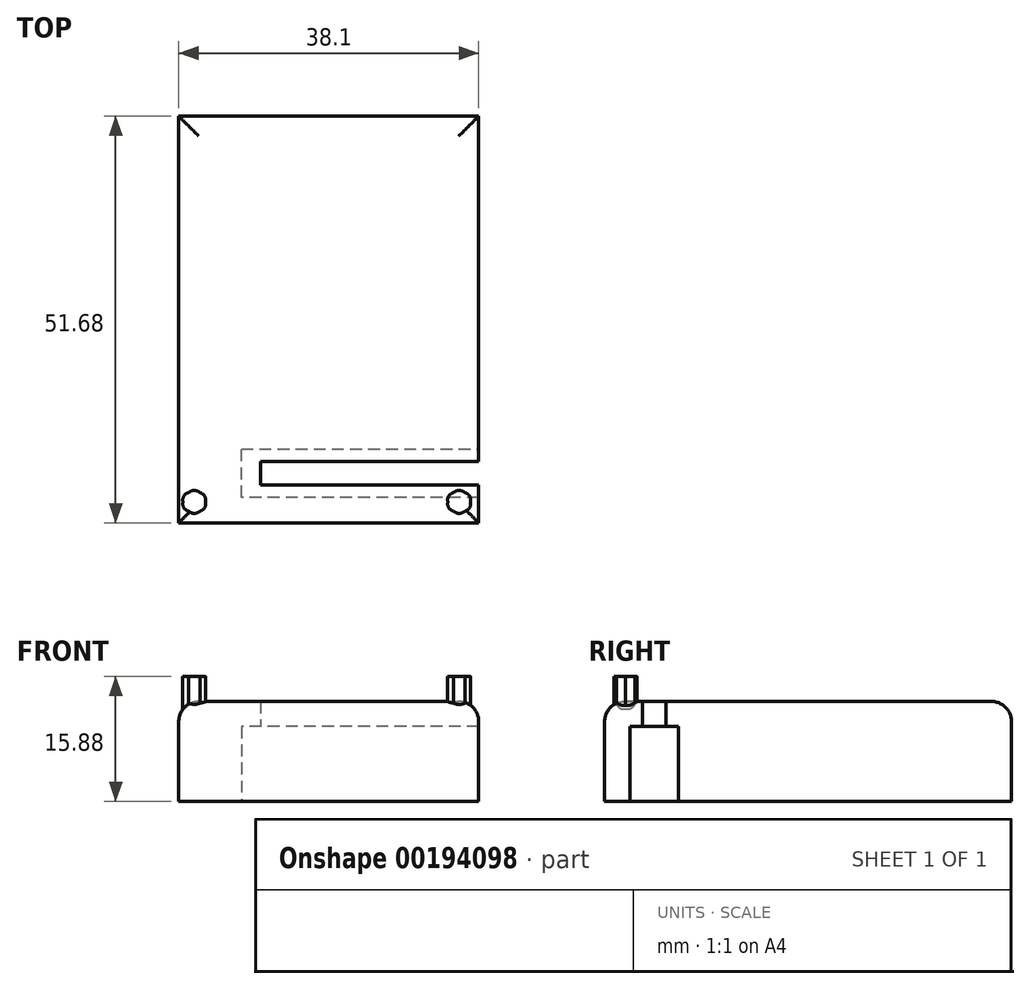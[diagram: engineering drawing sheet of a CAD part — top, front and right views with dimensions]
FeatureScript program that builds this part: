
annotation { "Feature Type Name" : "Feature", "Feature Type Description" : "" }
export const myFeature = defineFeature(function(context is Context, id is Id, definition is map)
    precondition{}
    {
        {
            var Q0;
            Q0=qCreatedBy(makeId("Top.planeOp"),FACE);
            var sketch = newSketch(context, id + "F0", { "sketchPlane" : qUnion([Q0])});
            skFitSpline(sketch, "E0", {"points": [v(-17.28, -23.17) * mm, v(-17.28, -23.66) * mm, v(-17.56, -24.1) * mm, v(-18, -24.35) * mm]});
            skFitSpline(sketch, "E1", {"points": [v(-18, -24.35) * mm, v(-18.45, -24.6) * mm, v(-19, -24.6) * mm, v(-19.44, -24.35) * mm]});
            skFitSpline(sketch, "E2", {"points": [v(-19.44, -24.35) * mm, v(-19.88, -24.1) * mm, v(-20.16, -23.66) * mm, v(-20.16, -23.17) * mm]});
            skFitSpline(sketch, "E3", {"points": [v(-20.16, -23.17) * mm, v(-20.16, -22.68) * mm, v(-19.88, -22.23) * mm, v(-19.44, -21.98) * mm]});
            skFitSpline(sketch, "E4", {"points": [v(-19.44, -21.98) * mm, v(-19, -21.74) * mm, v(-18.45, -21.74) * mm, v(-18, -21.98) * mm]});
            skFitSpline(sketch, "E5", {"points": [v(-18, -21.98) * mm, v(-17.56, -22.23) * mm, v(-17.28, -22.68) * mm, v(-17.28, -23.17) * mm]});
            skFitSpline(sketch, "E6", {"points": [v(16.37, -23.17) * mm, v(16.37, -23.66) * mm, v(16.1, -24.1) * mm, v(15.65, -24.35) * mm]});
            skFitSpline(sketch, "E7", {"points": [v(15.65, -24.35) * mm, v(15.2, -24.6) * mm, v(14.66, -24.6) * mm, v(14.21, -24.35) * mm]});
            skFitSpline(sketch, "E8", {"points": [v(14.21, -24.35) * mm, v(13.77, -24.1) * mm, v(13.5, -23.66) * mm, v(13.5, -23.17) * mm]});
            skFitSpline(sketch, "E9", {"points": [v(13.5, -23.17) * mm, v(13.5, -22.68) * mm, v(13.77, -22.23) * mm, v(14.21, -21.98) * mm]});
            skFitSpline(sketch, "E10", {"points": [v(14.21, -21.98) * mm, v(14.66, -21.74) * mm, v(15.2, -21.74) * mm, v(15.65, -21.98) * mm]});
            skFitSpline(sketch, "E11", {"points": [v(15.65, -21.98) * mm, v(16.1, -22.23) * mm, v(16.37, -22.68) * mm, v(16.37, -23.17) * mm]});
            skLineSegment(sketch, "E12", {"start": v(-10.31, -18.02) * mm, "end": v(17.41, -18.02) * mm});
            skLineSegment(sketch, "E13", {"start": v(-10.31, -21.04) * mm, "end": v(-10.31, -18.02) * mm});
            skLineSegment(sketch, "E14", {"start": v(-12.73, -16.46) * mm, "end": v(17.41, -16.46) * mm});
            skLineSegment(sketch, "E15", {"start": v(17.41, -22.6) * mm, "end": v(-12.73, -22.6) * mm});
            skLineSegment(sketch, "E16", {"start": v(-12.73, -22.6) * mm, "end": v(-12.73, -16.46) * mm});
            skLineSegment(sketch, "E17", {"start": v(-20.69, 25.84) * mm, "end": v(17.41, 25.84) * mm});
            skLineSegment(sketch, "E18", {"start": v(17.41, 24.96) * mm, "end": v(17.41, -25.84) * mm});
            skLineSegment(sketch, "E19", {"start": v(17.41, -25.84) * mm, "end": v(-20.69, -25.84) * mm});
            skLineSegment(sketch, "E20", {"start": v(-20.69, -25.84) * mm, "end": v(-20.69, 24.96) * mm});
            skLineSegment(sketch, "E21.trimOffspring", {"start": v(17.41, -21.04) * mm, "end": v(-10.31, -21.04) * mm});
            skLineSegment(sketch, "E22", {"start": v(17.41, 24.96) * mm, "end": v(17.41, 25.84) * mm});
            skLineSegment(sketch, "E23", {"start": v(-20.69, 24.96) * mm, "end": v(-20.69, 25.84) * mm});
            skSolve(sketch);
        }
        {
            var Q0;
            Q0=makeQuery(id+"F0.imprint","IMPRINT",FACE,{"disambiguationData":[TD([[makeQuery(id+"F0.imprint","IMPRINT",EDGE,{"derivedFrom":sQuery(id+"F0.wireOp",EDGE,"E0")}),1.0]])]});
            var Q1;
            {var subQ10=sQuery(id+"F0.wireOp",EDGE,"E10");Q1=makeQuery(id+"F0.imprint","IMPRINT",FACE,{"disambiguationData":[TD([[makeQuery(id+"F0.imprint","IMPRINT",EDGE,{"derivedFrom":subQ10}),1.0]])]});}
            var Q2;
            {var subQ0=sQuery(id+"F0.wireOp",EDGE,"E12");Q2=makeQuery(id+"F0.imprint","IMPRINT",FACE,{"disambiguationData":[TD([[makeQuery(id+"F0.imprint","IMPRINT",EDGE,{"derivedFrom":subQ0}),-1.0]])]});}
            var Q3;
            {var subQ6=sQuery(id+"F0.wireOp",EDGE,"E6");Q3=makeQuery(id+"F0.imprint","IMPRINT",FACE,{"disambiguationData":[TD([[makeQuery(id+"F0.imprint","IMPRINT",EDGE,{"derivedFrom":subQ6}),-1.0]])]});}
            var Q4;
            {var subQ0=sQuery(id+"F0.wireOp",EDGE,"E10");Q4=makeQuery(id+"F0.imprint","IMPRINT",FACE,{"disambiguationData":[TD([[makeQuery(id+"F0.imprint","IMPRINT",EDGE,{"derivedFrom":subQ0}),-1.0]])]});}
            var Q5;
            Q5=makeQuery(id+"F0.imprint","IMPRINT",FACE,{"disambiguationData":[TD([[makeQuery(id+"F0.imprint","IMPRINT",EDGE,{"derivedFrom":sQuery(id+"F0.wireOp",EDGE,"E0")}),-1.0]])]});
            extrude(context, id + "F1", {"entities" : qUnion([Q0, Q1, Q2, Q3, Q4, Q5]), "depth" : 12.7 * mm});
        }
        {
            var Q0;
            {var subQ10=sQuery(id+"F0.wireOp",EDGE,"E10");Q0=makeQuery(id+"F0.imprint","IMPRINT",FACE,{"disambiguationData":[TD([[makeQuery(id+"F0.imprint","IMPRINT",EDGE,{"derivedFrom":subQ10}),1.0]])]});}
            var Q1;
            {var subQ0=sQuery(id+"F0.wireOp",EDGE,"E10");Q1=makeQuery(id+"F0.imprint","IMPRINT",FACE,{"disambiguationData":[TD([[makeQuery(id+"F0.imprint","IMPRINT",EDGE,{"derivedFrom":subQ0}),-1.0]])]});}
            var Q2;
            {var subQ0=sQuery(id+"F0.wireOp",EDGE,"E12");Q2=makeQuery(id+"F0.imprint","IMPRINT",FACE,{"disambiguationData":[TD([[makeQuery(id+"F0.imprint","IMPRINT",EDGE,{"derivedFrom":subQ0}),-1.0]])]});}
            extrude(context, id + "F2", {"entities" : qUnion([Q0, Q1, Q2]), "operationType" : NewBodyOperationType.REMOVE, "depth" : 9.52 * mm});
        }
        {
            var Q0;
            {var subQ0=sQuery(id+"F0.wireOp",EDGE,"E12");Q0=makeQuery(id+"F0.imprint","IMPRINT",FACE,{"disambiguationData":[TD([[makeQuery(id+"F0.imprint","IMPRINT",EDGE,{"derivedFrom":subQ0}),-1.0]])]});}
            extrude(context, id + "F3", {"entities" : qUnion([Q0]), "operationType" : NewBodyOperationType.REMOVE, "depth" : 25.4 * mm});
        }
        {
            var Q0;
            {var subQ6=sQuery(id+"F0.wireOp",EDGE,"E6");Q0=makeQuery(id+"F0.imprint","IMPRINT",FACE,{"disambiguationData":[TD([[makeQuery(id+"F0.imprint","IMPRINT",EDGE,{"derivedFrom":subQ6}),-1.0]])]});}
            var Q1;
            Q1=makeQuery(id+"F0.imprint","IMPRINT",FACE,{"disambiguationData":[TD([[makeQuery(id+"F0.imprint","IMPRINT",EDGE,{"derivedFrom":sQuery(id+"F0.wireOp",EDGE,"E0")}),-1.0]])]});
            var Q2;
            {var subQ0=sQuery(id+"F0.wireOp",EDGE,"E10");Q2=makeQuery(id+"F0.imprint","IMPRINT",FACE,{"disambiguationData":[TD([[makeQuery(id+"F0.imprint","IMPRINT",EDGE,{"derivedFrom":subQ0}),-1.0]])]});}
            extrude(context, id + "F4", {"entities" : qUnion([Q0, Q1, Q2]), "operationType" : NewBodyOperationType.ADD, "depth" : 15.88 * mm});
        }
        {
            var Q0;
            {var subQ0=sQuery(id+"F0.wireOp",EDGE,"E10");Q0=makeQuery(id+"F0.imprint","IMPRINT",FACE,{"disambiguationData":[TD([[makeQuery(id+"F0.imprint","IMPRINT",EDGE,{"derivedFrom":subQ0}),-1.0]])]});}
            extrude(context, id + "F5", {"entities" : qUnion([Q0]), "operationType" : NewBodyOperationType.REMOVE, "depth" : 9.52 * mm});
        }
        {
            var Q0;
            Q0=makeQuery(id+"F1.opExtrude","CAP_EDGE",EDGE,{"disambiguationData":[OSD([sQuery(id+"F0.wireOp",EDGE,"E20"),sQuery(id+"F0.wireOp",EDGE,"E23")])],"isStart":false});
            var Q1;
            Q1=makeQuery(id+"F1.opExtrude","CAP_EDGE",EDGE,{"disambiguationData":[OSD([sQuery(id+"F0.wireOp",EDGE,"E17")])],"isStart":false});
            var Q2;
            Q2=makeQuery(id+"F1.opExtrude","CAP_EDGE",EDGE,{"disambiguationData":[OSD([sQuery(id+"F0.wireOp",EDGE,"E19")])],"isStart":false});
            var Q3;
            {var subQ0=sQuery(id+"F0.wireOp",EDGE,"E17");var subQ1=sQuery(id+"F0.wireOp",EDGE,"E22");var subQ2=sQuery(id+"F0.wireOp",EDGE,"E18");Q3=makeQuery(id+"F3.boolean.opBoolean","SPLIT",EDGE,{"disambiguationData":[TD([makeQuery(id+"F1.opExtrude","SWEPT_FACE",FACE,{"disambiguationData":[OSD([subQ0])]})])],"derivedFrom":makeQuery(id+"F1.opExtrude","CAP_EDGE",EDGE,{"disambiguationData":[OSD([subQ2,subQ1])],"isStart":false})});}
            var Q4;
            {var subQ0=sQuery(id+"F0.wireOp",EDGE,"E22");var subQ1=sQuery(id+"F0.wireOp",EDGE,"E19");var subQ2=sQuery(id+"F0.wireOp",EDGE,"E18");Q4=makeQuery(id+"F3.boolean.opBoolean","SPLIT",EDGE,{"disambiguationData":[TD([makeQuery(id+"F1.opExtrude","SWEPT_FACE",FACE,{"disambiguationData":[OSD([subQ1])]})])],"derivedFrom":makeQuery(id+"F1.opExtrude","CAP_EDGE",EDGE,{"disambiguationData":[OSD([subQ2,subQ0])],"isStart":false})});}
            fillet(context, id + "F6", {"entities" : qUnion([Q0, Q1, Q2, Q3, Q4]), "radius" : 2.54 * mm, "tangentPropagation" : true, "allowEdgeOverflow" : false});
        }
    });
